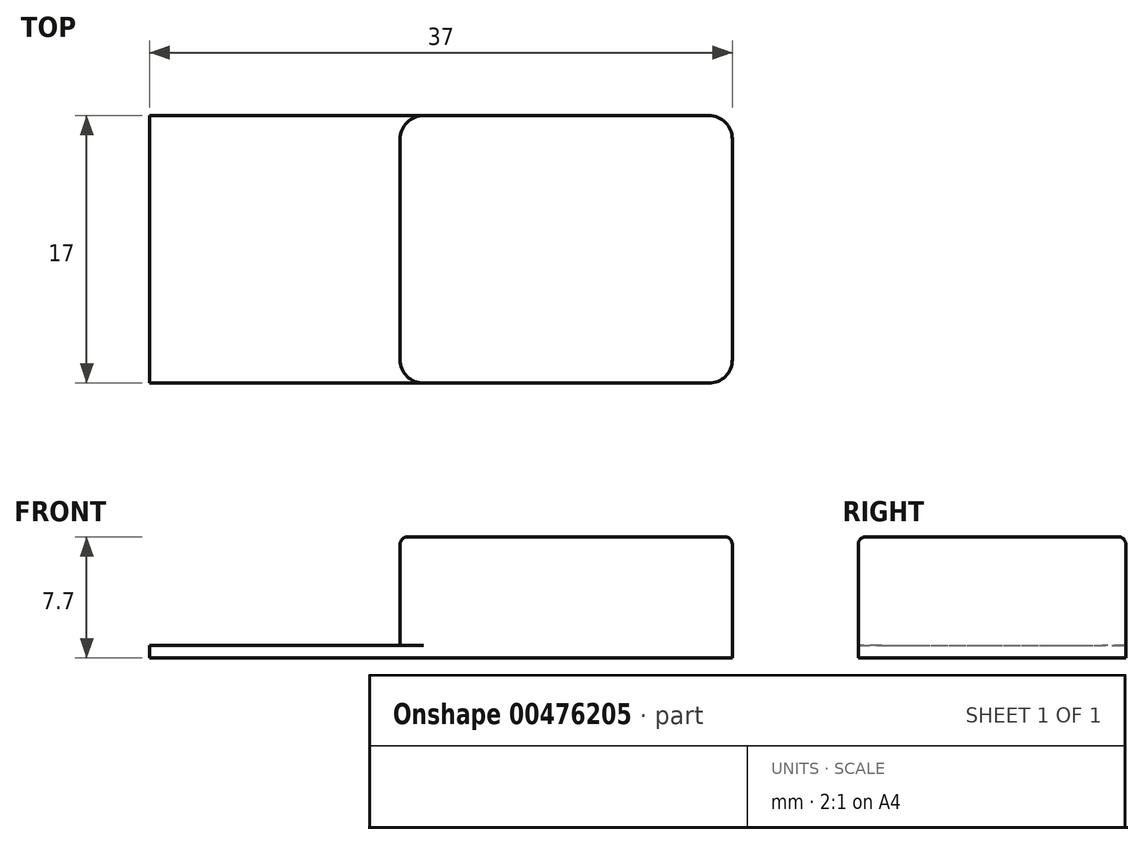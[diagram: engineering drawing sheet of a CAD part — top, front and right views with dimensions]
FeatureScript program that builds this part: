
annotation { "Feature Type Name" : "Feature", "Feature Type Description" : "" }
export const myFeature = defineFeature(function(context is Context, id is Id, definition is map)
    precondition{}
    {
        {
            var Q0;
            Q0=qCreatedBy(makeId("Top.planeOp"),FACE);
            var sketch = newSketch(context, id + "F0", { "sketchPlane" : qUnion([Q0])});
            skLineSegment(sketch, "E0.bottom", {"start": v(18.5, -8.5) * mm, "end": v(-18.5, -8.5) * mm});
            skLineSegment(sketch, "E0.top", {"start": v(18.5, 8.5) * mm, "end": v(-18.5, 8.5) * mm});
            skLineSegment(sketch, "E0.left", {"start": v(18.5, -8.5) * mm, "end": v(18.5, 8.5) * mm});
            skLineSegment(sketch, "E0.right", {"start": v(-18.5, -8.5) * mm, "end": v(-18.5, 8.5) * mm});
            skPoint(sketch, "E0.middle", {"position": v(0, 0) * mm});
            skSolve(sketch);
        }
        {
            var Q0;
            Q0=makeQuery(id+"F0.imprint","IMPRINT",FACE,{"disambiguationData":[TD([[makeQuery(id+"F0.imprint","IMPRINT",EDGE,{"derivedFrom":sQuery(id+"F0.wireOp",EDGE,"E0.bottom")}),-1.0]])]});
            extrude(context, id + "F1", {"entities" : qUnion([Q0]), "depth" : .8 * mm});
        }
        {
            var Q0;
            Q0=makeQuery(id+"F1.opExtrude","CAP_FACE",FACE,{"disambiguationData":[OSD([sQuery(id+"F0.wireOp",EDGE,"E0.bottom"),sQuery(id+"F0.wireOp",EDGE,"E0.top"),sQuery(id+"F0.wireOp",EDGE,"E0.left"),sQuery(id+"F0.wireOp",EDGE,"E0.right")])],"isStart":false});
            var sketch = newSketch(context, id + "F2", { "sketchPlane" : qUnion([Q0])});
            skLineSegment(sketch, "E1", {"start": v(-18.5, 0) * mm, "end": v(18.5, 0) * mm});
            skLineSegment(sketch, "E2.bottom", {"start": v(18.5, -8.5) * mm, "end": v(-2.6, -8.5) * mm});
            skLineSegment(sketch, "E2.top", {"start": v(18.5, 8.5) * mm, "end": v(-2.6, 8.5) * mm});
            skLineSegment(sketch, "E2.left", {"start": v(18.5, -8.5) * mm, "end": v(18.5, 8.5) * mm});
            skLineSegment(sketch, "E2.right", {"start": v(-2.6, -8.5) * mm, "end": v(-2.6, 8.5) * mm});
            skPoint(sketch, "E2.middle", {"position": v(7.95, 0) * mm});
            skSolve(sketch);
        }
        {
            var Q0;
            {var subQ5=sQuery(id+"F2.wireOp",EDGE,"E2.top");Q0=makeQuery(id+"F2.imprint","IMPRINT",FACE,{"disambiguationData":[TD([[makeQuery(id+"F2.imprint","IMPRINT",EDGE,{"derivedFrom":subQ5}),1.0]])]});}
            var Q1;
            {var subQ5=sQuery(id+"F2.wireOp",EDGE,"E2.bottom");Q1=makeQuery(id+"F2.imprint","IMPRINT",FACE,{"disambiguationData":[TD([[makeQuery(id+"F2.imprint","IMPRINT",EDGE,{"derivedFrom":subQ5}),-1.0]])]});}
            extrude(context, id + "F3", {"entities" : qUnion([Q0, Q1]), "operationType" : NewBodyOperationType.ADD, "depth" : 6.9 * mm});
        }
        {
            var Q0;
            Q0=makeQuery(id+"F3.boolean.opBoolean","MERGE",EDGE,{"derivedFrom":[makeQuery(id+"F1.opExtrude","SWEPT_EDGE",EDGE,{"disambiguationData":[OSD([sQuery(id+"F0.wireOp",EDGE,"E0.bottom"),sQuery(id+"F0.wireOp",EDGE,"E0.left")])]}),makeQuery(id+"F3.opExtrude","SWEPT_EDGE",EDGE,{"disambiguationData":[OSD([sQuery(id+"F2.wireOp",EDGE,"E2.bottom"),sQuery(id+"F2.wireOp",EDGE,"E2.left")])]})]});
            var Q1;
            Q1=makeQuery(id+"F3.boolean.opBoolean","MERGE",EDGE,{"derivedFrom":[makeQuery(id+"F1.opExtrude","SWEPT_EDGE",EDGE,{"disambiguationData":[OSD([sQuery(id+"F0.wireOp",EDGE,"E0.top"),sQuery(id+"F0.wireOp",EDGE,"E0.left")])]}),makeQuery(id+"F3.opExtrude","SWEPT_EDGE",EDGE,{"disambiguationData":[OSD([sQuery(id+"F2.wireOp",EDGE,"E2.top"),sQuery(id+"F2.wireOp",EDGE,"E2.left")])]})]});
            var Q2;
            Q2=makeQuery(id+"F3.opExtrude","SWEPT_EDGE",EDGE,{"disambiguationData":[OSD([sQuery(id+"F0.wireOp",EDGE,"E0.top"),sQuery(id+"F2.wireOp",EDGE,"E2.top"),sQuery(id+"F2.wireOp",EDGE,"E2.right")])]});
            var Q3;
            Q3=makeQuery(id+"F3.opExtrude","SWEPT_EDGE",EDGE,{"disambiguationData":[OSD([sQuery(id+"F0.wireOp",EDGE,"E0.bottom"),sQuery(id+"F2.wireOp",EDGE,"E2.bottom"),sQuery(id+"F2.wireOp",EDGE,"E2.right")])]});
            fillet(context, id + "F4", {"entities" : qUnion([Q0, Q1, Q2, Q3]), "radius" : 1.5 * mm, "tangentPropagation" : true, "allowEdgeOverflow" : false});
        }
        {
            var Q0;
            Q0=makeQuery(id+"F3.opExtrude","CAP_EDGE",EDGE,{"disambiguationData":[OSD([sQuery(id+"F2.wireOp",EDGE,"E2.top")])],"isStart":false});
            fillet(context, id + "F5", {"entities" : qUnion([Q0]), "radius" : .5 * mm, "tangentPropagation" : true, "allowEdgeOverflow" : false});
        }
    });
